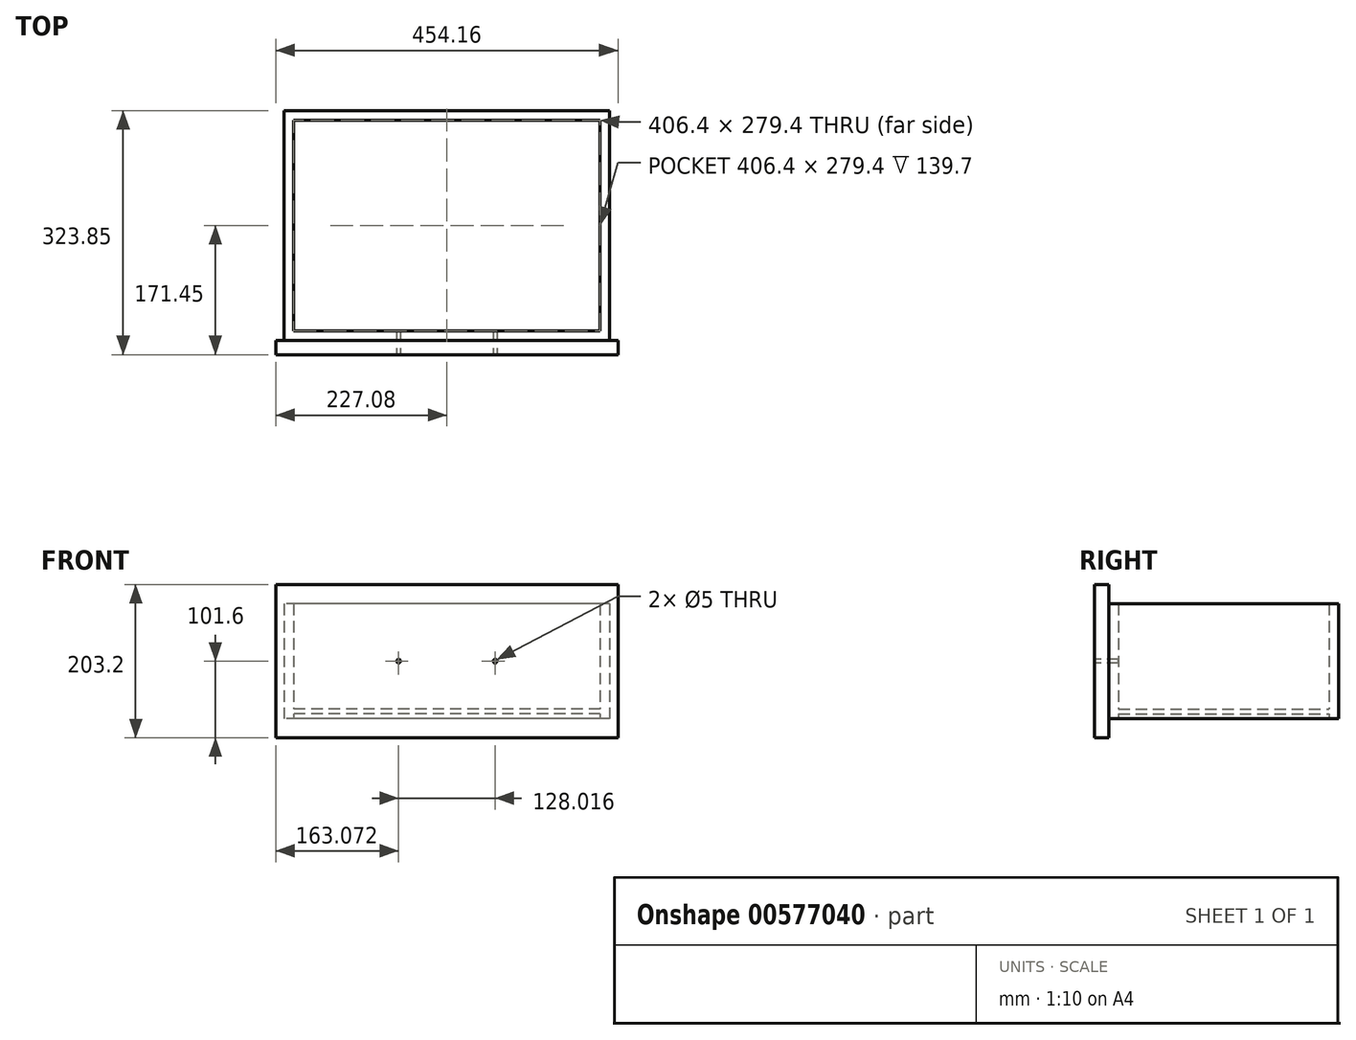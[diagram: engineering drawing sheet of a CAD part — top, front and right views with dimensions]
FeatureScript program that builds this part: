
annotation { "Feature Type Name" : "Feature", "Feature Type Description" : "" }
export const myFeature = defineFeature(function(context is Context, id is Id, definition is map)
    precondition{}
    {
        {
            var Q0;
            Q0=qCreatedBy(makeId("Top.planeOp"),FACE);
            var sketch = newSketch(context, id + "F0", { "sketchPlane" : qUnion([Q0])});
            skLineSegment(sketch, "E0.bottom", {"start": v(215.9, 152.4) * mm, "end": v(-215.9, 152.4) * mm});
            skLineSegment(sketch, "E0.top", {"start": v(215.9, -152.4) * mm, "end": v(-215.9, -152.4) * mm});
            skLineSegment(sketch, "E0.left", {"start": v(215.9, 152.4) * mm, "end": v(215.9, -152.4) * mm});
            skLineSegment(sketch, "E0.right", {"start": v(-215.9, 152.4) * mm, "end": v(-215.9, -152.4) * mm});
            skPoint(sketch, "E0.middle", {"position": v(0, 0) * mm});
            skLineSegment(sketch, "E1.bottom", {"start": v(203.2, 139.7) * mm, "end": v(-203.2, 139.7) * mm});
            skLineSegment(sketch, "E1.top", {"start": v(203.2, -139.7) * mm, "end": v(-203.2, -139.7) * mm});
            skLineSegment(sketch, "E1.left", {"start": v(203.2, 139.7) * mm, "end": v(203.2, -139.7) * mm});
            skLineSegment(sketch, "E1.right", {"start": v(-203.2, 139.7) * mm, "end": v(-203.2, -139.7) * mm});
            skSolve(sketch);
        }
        {
            var Q0;
            Q0=makeQuery(id+"F0.imprint","IMPRINT",FACE,{"disambiguationData":[TD([[makeQuery(id+"F0.imprint","IMPRINT",EDGE,{"derivedFrom":sQuery(id+"F0.wireOp",EDGE,"E0.bottom")}),1.0]])]});
            extrude(context, id + "F1", {"entities" : qUnion([Q0]), "depth" : 152.4 * mm, "offsetDistance" : 25.4 * mm});
        }
        {
            var Q0;
            Q0=makeQuery(id+"F1.opExtrude","SWEPT_FACE",FACE,{"disambiguationData":[OSD([sQuery(id+"F0.wireOp",EDGE,"E1.right")])]});
            var sketch = newSketch(context, id + "F2", { "sketchPlane" : qUnion([Q0])});
            skLineSegment(sketch, "E2", {"start": v(-139.7, 0) * mm, "end": v(-139.7, 6.35) * mm});
            skLineSegment(sketch, "E3", {"start": v(-139.7, 6.35) * mm, "end": v(139.7, 6.35) * mm});
            skLineSegment(sketch, "E4", {"start": v(-139.7, 6.35) * mm, "end": v(-139.7, 12.7) * mm});
            skLineSegment(sketch, "E5", {"start": v(-139.7, 12.7) * mm, "end": v(139.7, 12.7) * mm});
            skSolve(sketch);
        }
        {
            var Q0;
            {var subQ0=sQuery(id+"F2.wireOp",EDGE,"E3");Q0=makeQuery(id+"F2.imprint","IMPRINT",FACE,{"disambiguationData":[TD([[makeQuery(id+"F2.imprint","IMPRINT",EDGE,{"derivedFrom":subQ0}),1.0]])]});}
            extrude(context, id + "F3", {"entities" : qUnion([Q0]), "operationType" : NewBodyOperationType.ADD, "endBound" : BoundingType.UP_TO_NEXT, "depth" : 25.4 * mm, "offsetDistance" : 25.4 * mm});
        }
        {
            var Q0;
            Q0=makeQuery(id+"F1.opExtrude","SWEPT_FACE",FACE,{"disambiguationData":[OSD([sQuery(id+"F0.wireOp",EDGE,"E0.top")])]});
            var sketch = newSketch(context, id + "F4", { "sketchPlane" : qUnion([Q0])});
            skLineSegment(sketch, "E6", {"start": v(0, 152.4) * mm, "end": v(0, 0) * mm});
            skLineSegment(sketch, "E7.bottom", {"start": v(227.08, 177.8) * mm, "end": v(-227.08, 177.8) * mm});
            skLineSegment(sketch, "E7.top", {"start": v(227.08, -25.4) * mm, "end": v(-227.08, -25.4) * mm});
            skLineSegment(sketch, "E7.left", {"start": v(227.08, 177.8) * mm, "end": v(227.08, -25.4) * mm});
            skLineSegment(sketch, "E7.right", {"start": v(-227.08, 177.8) * mm, "end": v(-227.08, -25.4) * mm});
            skPoint(sketch, "E7.middle", {"position": v(0, 76.2) * mm});
            skSolve(sketch);
        }
        {
            var Q0;
            Q0=qSketchRegion(id+"F4",true);
            extrude(context, id + "F5", {"entities" : qUnion([Q0]), "operationType" : NewBodyOperationType.ADD, "depth" : 19.05 * mm, "offsetDistance" : 25.4 * mm});
        }
        {
            var Q0;
            Q0=makeQuery(id+"F5.opExtrude","CAP_FACE",FACE,{"disambiguationData":[OSD([sQuery(id+"F4.wireOp",EDGE,"E7.bottom"),sQuery(id+"F4.wireOp",EDGE,"E7.top"),sQuery(id+"F4.wireOp",EDGE,"E7.left"),sQuery(id+"F4.wireOp",EDGE,"E7.right")])],"isStart":false});
            var sketch = newSketch(context, id + "F6", { "sketchPlane" : qUnion([Q0])});
            skLineSegment(sketch, "E8", {"start": v(0, 177.8) * mm, "end": v(0, 76.2) * mm});
            skLineSegment(sketch, "E9", {"start": v(0, 76.2) * mm, "end": v(64, 76.2) * mm});
            skLineSegment(sketch, "E10", {"start": v(0, 76.2) * mm, "end": v(-64, 76.2) * mm});
            skPoint(sketch, "E11", {"position": v(-64, 76.2) * mm});
            skPoint(sketch, "E12", {"position": v(64, 76.2) * mm});
            skSolve(sketch);
        }
        {
            var Q0;
            Q0=sQuery(id+"F6.wireOp",VERTEX,"E11");
            var Q1;
            Q1=sQuery(id+"F6.wireOp",VERTEX,"E12");
            var Q2;
            Q2=makeQuery(id+"F1.opExtrude","SWEPT_BODY",BODY,{"disambiguationData":[OSD([sQuery(id+"F0.wireOp",EDGE,"E0.bottom"),sQuery(id+"F0.wireOp",EDGE,"E0.top"),sQuery(id+"F0.wireOp",EDGE,"E0.left"),sQuery(id+"F0.wireOp",EDGE,"E0.right"),sQuery(id+"F0.wireOp",EDGE,"E1.bottom"),sQuery(id+"F0.wireOp",EDGE,"E1.top"),sQuery(id+"F0.wireOp",EDGE,"E1.left"),sQuery(id+"F0.wireOp",EDGE,"E1.right")])]});
            hole(context, id + "F7", {"style" : HoleStyle.SIMPLE, "endStyle" : HoleEndStyle.BLIND, "holeDiameter" : 5 * mm, "majorDiameter" : 6.35 * mm, "holeDepth" : 31.75 * mm, "isTappedThrough" : true, "tappedDepth" : 12.7 * mm, "tapClearance" : 3, "startFromSketch" : true, "locations" : qUnion([Q0, Q1]), "scope" : qUnion([Q2])});
        }
    });
